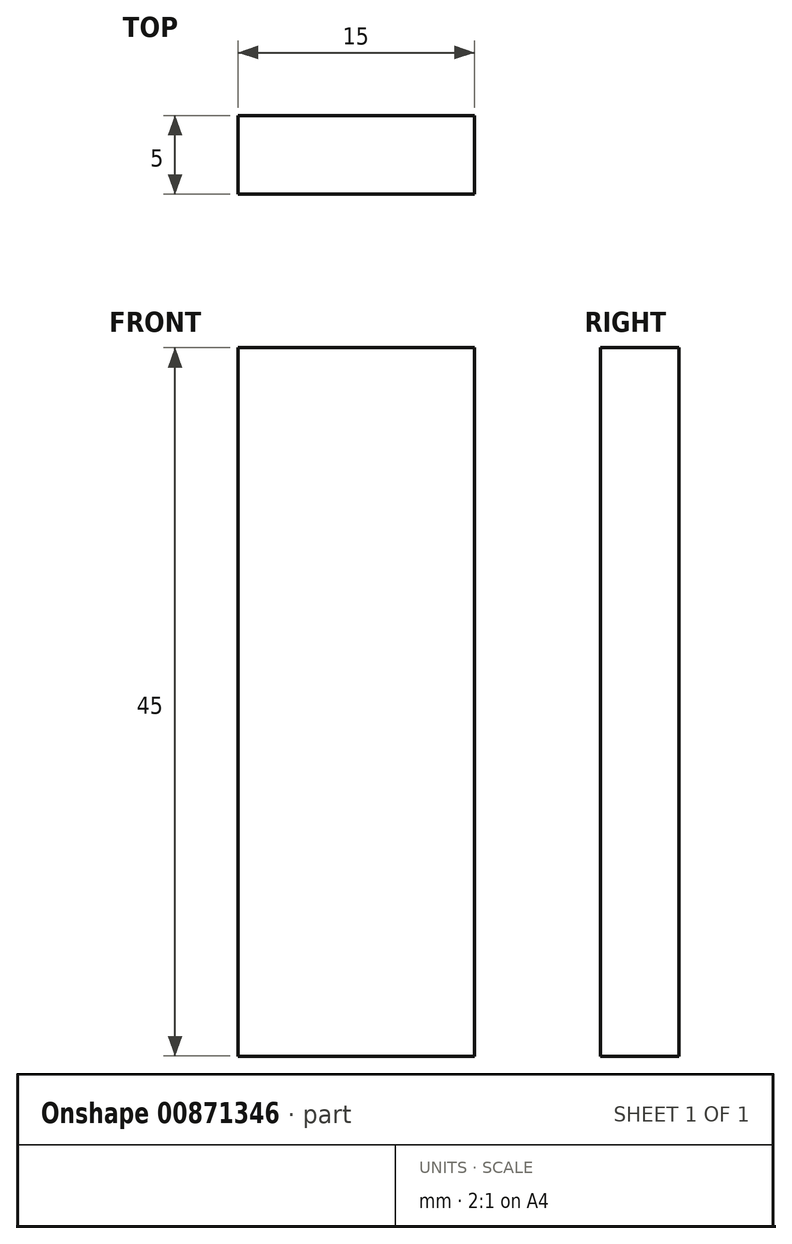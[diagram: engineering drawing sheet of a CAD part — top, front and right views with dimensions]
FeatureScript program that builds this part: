
annotation { "Feature Type Name" : "Feature", "Feature Type Description" : "" }
export const myFeature = defineFeature(function(context is Context, id is Id, definition is map)
    precondition{}
    {
        {
            var Q0;
            Q0=qCreatedBy(makeId("Front.planeOp"),FACE);
            var sketch = newSketch(context, id + "F0", { "sketchPlane" : qUnion([Q0])});
            skLineSegment(sketch, "E0.bottom", {"start": v(-33.97, 49.18) * mm, "end": v(-18.97, 49.18) * mm});
            skLineSegment(sketch, "E0.top", {"start": v(-33.97, 4.18) * mm, "end": v(-18.97, 4.18) * mm});
            skLineSegment(sketch, "E0.left", {"start": v(-33.97, 49.18) * mm, "end": v(-33.97, 4.18) * mm});
            skLineSegment(sketch, "E0.right", {"start": v(-18.97, 49.18) * mm, "end": v(-18.97, 4.18) * mm});
            skSolve(sketch);
        }
        {
            var Q0;
            Q0=makeQuery(id+"F0.imprint","IMPRINT",FACE,{"disambiguationData":[TD([[makeQuery(id+"F0.imprint","IMPRINT",EDGE,{"derivedFrom":sQuery(id+"F0.wireOp",EDGE,"E0.bottom")}),-1.0]])]});
            extrude(context, id + "F1", {"entities" : qUnion([Q0]), "depth" : 5 * mm, "offsetDistance" : 25 * mm});
        }
    });
